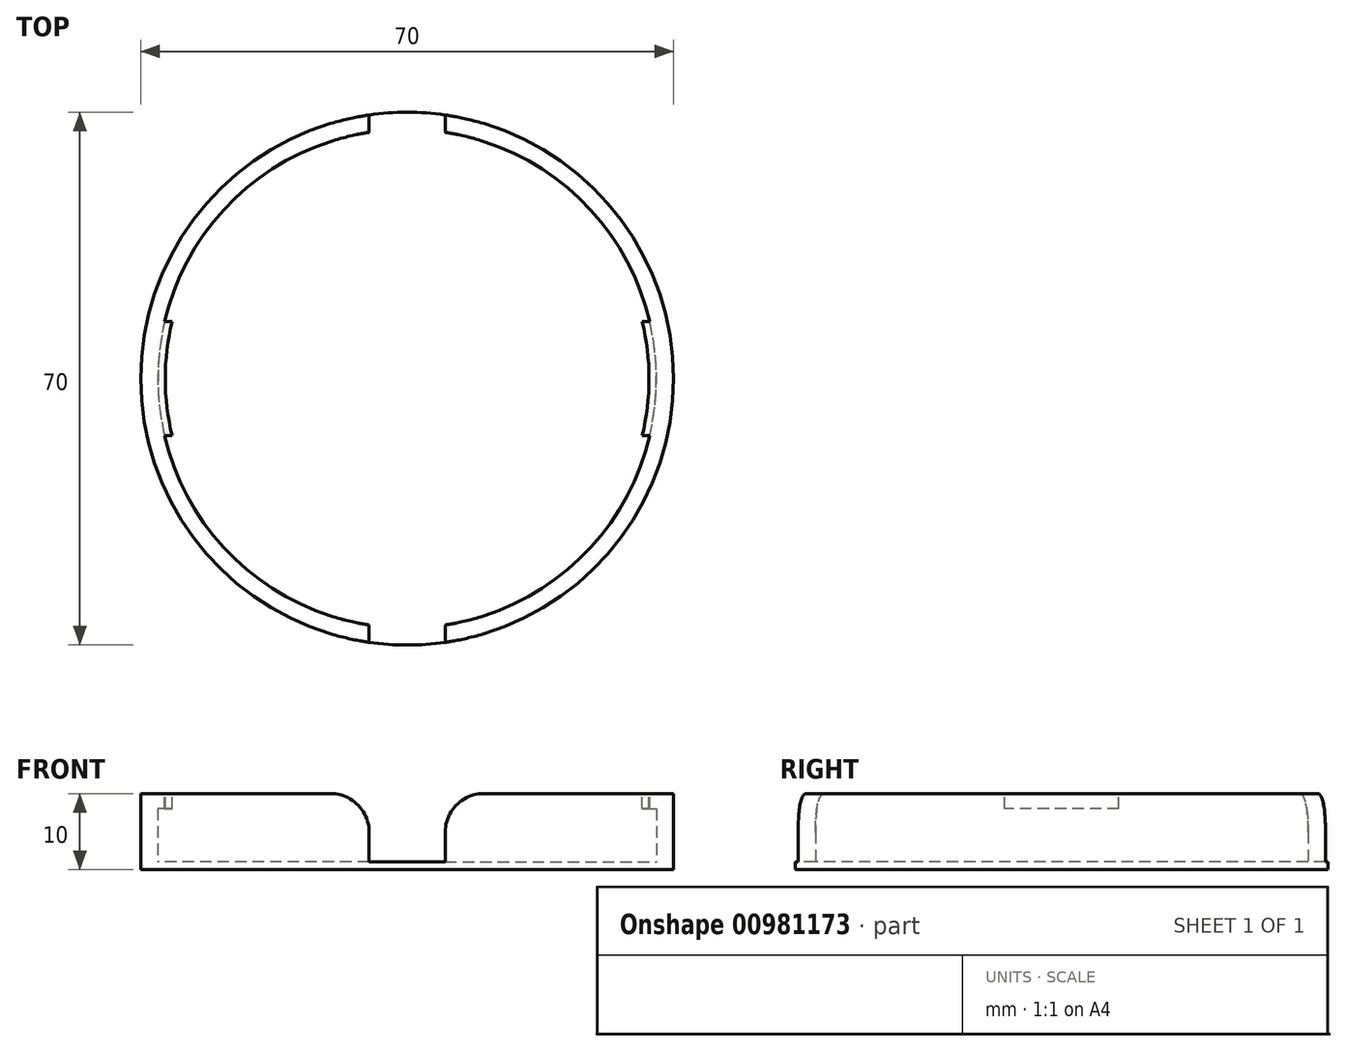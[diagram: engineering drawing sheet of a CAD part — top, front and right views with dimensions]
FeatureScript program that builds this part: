
annotation { "Feature Type Name" : "Feature", "Feature Type Description" : "" }
export const myFeature = defineFeature(function(context is Context, id is Id, definition is map)
    precondition{}
    {
        {
            var Q0;
            Q0=qCreatedBy(makeId("Top.planeOp"),FACE);
            var sketch = newSketch(context, id + "F0", { "sketchPlane" : qUnion([Q0])});
            skCircle(sketch, "E0", {"center": v(0, 0) * mm, "radius": 35 * mm});
            skSolve(sketch);
        }
        {
            var Q0;
            Q0 = qSketchRegion(id + "F0", true);
            extrude(context, id + "F1", {"entities" : qUnion([Q0]), "oppositeDirection" : true, "depth" : 1 * mm, "offsetDistance" : 25.4 * mm});
        }
        {
            var Q0;
            Q0=qCreatedBy(makeId("Top.planeOp"),FACE);
            var sketch = newSketch(context, id + "F2", { "sketchPlane" : qUnion([Q0])});
            skCircle(sketch, "E1", {"center": v(0, 0) * mm, "radius": 32.75 * mm});
            skCircle(sketch, "E2", {"center": v(0, 0) * mm, "radius": 35 * mm});
            skSolve(sketch);
        }
        {
            var Q0;
            Q0 = qSketchRegion(id + "F2", true);
            extrude(context, id + "F3", {"entities" : qUnion([Q0]), "operationType" : NewBodyOperationType.ADD, "depth" : 9 * mm, "offsetDistance" : 25.4 * mm});
        }
        {
            var Q0;
            Q0=makeQuery(id+"F3.opExtrude","CAP_FACE",FACE,{"disambiguationData":[OSD([sQuery(id+"F2.wireOp",EDGE,"E1"),sQuery(id+"F2.wireOp",EDGE,"E2")])],"isStart":false});
            var sketch = newSketch(context, id + "F4", { "sketchPlane" : qUnion([Q0])});
            skArc(sketch, "E3", {"start": v(-32.75, 0) * mm, "mid": v(-32.53, -3.78) * mm, "end": v(-31.88, -7.5) * mm});
            skLineSegment(sketch, "E4", {"start": v(-32.75, 0) * mm, "end": v(0, 0) * mm, "construction": true});
            skArc(sketch, "E5.MirrorCS", {"start": v(-32.75, 0) * mm, "mid": v(-32.53, 3.78) * mm, "end": v(-31.88, 7.5) * mm});
            skArc(sketch, "E6", {"start": v(-30.88, 7.5) * mm, "mid": v(-31.78, 0) * mm, "end": v(-30.88, -7.5) * mm});
            skLineSegment(sketch, "E7", {"start": v(-31.88, 7.5) * mm, "end": v(-30.88, 7.5) * mm});
            skLineSegment(sketch, "E8", {"start": v(-31.88, -7.5) * mm, "end": v(-30.88, -7.5) * mm});
            skLineSegment(sketch, "E9", {"start": v(0, 0) * mm, "end": v(0, 32.75) * mm, "construction": true});
            skLineSegment(sketch, "E10.MirrorCS", {"start": v(31.88, -7.5) * mm, "end": v(30.88, -7.5) * mm});
            skArc(sketch, "E11.MirrorCS", {"start": v(32.75, 0) * mm, "mid": v(32.53, -3.78) * mm, "end": v(31.88, -7.5) * mm});
            skArc(sketch, "E12.MirrorCS", {"start": v(32.75, 0) * mm, "mid": v(32.53, 3.78) * mm, "end": v(31.88, 7.5) * mm});
            skArc(sketch, "E13.MirrorCS", {"start": v(30.88, 7.5) * mm, "mid": v(31.78, 0) * mm, "end": v(30.88, -7.5) * mm});
            skLineSegment(sketch, "E14.MirrorCS", {"start": v(31.88, 7.5) * mm, "end": v(30.88, 7.5) * mm});
            skSolve(sketch);
        }
        {
            var Q0;
            Q0 = qSketchRegion(id + "F4", true);
            extrude(context, id + "F5", {"entities" : qUnion([Q0]), "operationType" : NewBodyOperationType.ADD, "oppositeDirection" : true, "depth" : 2 * mm, "offsetDistance" : 25.4 * mm});
        }
        {
            var Q0;
            Q0=qCreatedBy(makeId("Top.planeOp"),FACE);
            var sketch = newSketch(context, id + "F6", { "sketchPlane" : qUnion([Q0])});
            skLineSegment(sketch, "E15.bottom", {"start": v(5, 38.1) * mm, "end": v(-5, 38.1) * mm});
            skLineSegment(sketch, "E15.top", {"start": v(5, -38.1) * mm, "end": v(-5, -38.1) * mm});
            skLineSegment(sketch, "E15.left", {"start": v(5, 38.1) * mm, "end": v(5, -38.1) * mm});
            skLineSegment(sketch, "E15.right", {"start": v(-5, 38.1) * mm, "end": v(-5, -38.1) * mm});
            skPoint(sketch, "E15.middle", {"position": v(0, 0) * mm});
            skSolve(sketch);
        }
        {
            var Q0;
            Q0 = qSketchRegion(id + "F6", true);
            extrude(context, id + "F7", {"entities" : qUnion([Q0]), "operationType" : NewBodyOperationType.REMOVE, "depth" : 25.4 * mm, "offsetDistance" : 25.4 * mm});
        }
        {
            var Q0;
            Q0=makeQuery(id+"F7.boolean.opBoolean","INTERSECT",EDGE,{"disambiguationData":[OD(0.0)],"derivedFrom":[makeQuery(id+"F5.boolean.opBoolean","MERGE",FACE,{"derivedFrom":[makeQuery(id+"F3.opExtrude","CAP_FACE",FACE,{"disambiguationData":[OSD([sQuery(id+"F2.wireOp",EDGE,"E1"),sQuery(id+"F2.wireOp",EDGE,"E2")])],"isStart":false}),makeQuery(id+"F5.opExtrude","CAP_FACE",FACE,{"disambiguationData":[OSD([sQuery(id+"F4.wireOp",EDGE,"E3"),sQuery(id+"F4.wireOp",EDGE,"E5.MirrorCS"),sQuery(id+"F4.wireOp",EDGE,"E6"),sQuery(id+"F4.wireOp",EDGE,"E7"),sQuery(id+"F4.wireOp",EDGE,"E8")])],"isStart":true}),makeQuery(id+"F5.opExtrude","CAP_FACE",FACE,{"disambiguationData":[OSD([sQuery(id+"F4.wireOp",EDGE,"E10.MirrorCS"),sQuery(id+"F4.wireOp",EDGE,"E11.MirrorCS"),sQuery(id+"F4.wireOp",EDGE,"E12.MirrorCS"),sQuery(id+"F4.wireOp",EDGE,"E13.MirrorCS"),sQuery(id+"F4.wireOp",EDGE,"E14.MirrorCS")])],"isStart":true})]}),makeQuery(id+"F7.opExtrude","SWEPT_FACE",FACE,{"disambiguationData":[OSD([sQuery(id+"F6.wireOp",EDGE,"E15.right")])]})]});
            var Q1;
            Q1=makeQuery(id+"F7.boolean.opBoolean","INTERSECT",EDGE,{"disambiguationData":[OD(0.0)],"derivedFrom":[makeQuery(id+"F5.boolean.opBoolean","MERGE",FACE,{"derivedFrom":[makeQuery(id+"F3.opExtrude","CAP_FACE",FACE,{"disambiguationData":[OSD([sQuery(id+"F2.wireOp",EDGE,"E1"),sQuery(id+"F2.wireOp",EDGE,"E2")])],"isStart":false}),makeQuery(id+"F5.opExtrude","CAP_FACE",FACE,{"disambiguationData":[OSD([sQuery(id+"F4.wireOp",EDGE,"E3"),sQuery(id+"F4.wireOp",EDGE,"E5.MirrorCS"),sQuery(id+"F4.wireOp",EDGE,"E6"),sQuery(id+"F4.wireOp",EDGE,"E7"),sQuery(id+"F4.wireOp",EDGE,"E8")])],"isStart":true}),makeQuery(id+"F5.opExtrude","CAP_FACE",FACE,{"disambiguationData":[OSD([sQuery(id+"F4.wireOp",EDGE,"E10.MirrorCS"),sQuery(id+"F4.wireOp",EDGE,"E11.MirrorCS"),sQuery(id+"F4.wireOp",EDGE,"E12.MirrorCS"),sQuery(id+"F4.wireOp",EDGE,"E13.MirrorCS"),sQuery(id+"F4.wireOp",EDGE,"E14.MirrorCS")])],"isStart":true})]}),makeQuery(id+"F7.opExtrude","SWEPT_FACE",FACE,{"disambiguationData":[OSD([sQuery(id+"F6.wireOp",EDGE,"E15.left")])]})]});
            var Q2;
            Q2=makeQuery(id+"F7.boolean.opBoolean","INTERSECT",EDGE,{"disambiguationData":[OD(1.0)],"derivedFrom":[makeQuery(id+"F5.boolean.opBoolean","MERGE",FACE,{"derivedFrom":[makeQuery(id+"F3.opExtrude","CAP_FACE",FACE,{"disambiguationData":[OSD([sQuery(id+"F2.wireOp",EDGE,"E1"),sQuery(id+"F2.wireOp",EDGE,"E2")])],"isStart":false}),makeQuery(id+"F5.opExtrude","CAP_FACE",FACE,{"disambiguationData":[OSD([sQuery(id+"F4.wireOp",EDGE,"E3"),sQuery(id+"F4.wireOp",EDGE,"E5.MirrorCS"),sQuery(id+"F4.wireOp",EDGE,"E6"),sQuery(id+"F4.wireOp",EDGE,"E7"),sQuery(id+"F4.wireOp",EDGE,"E8")])],"isStart":true}),makeQuery(id+"F5.opExtrude","CAP_FACE",FACE,{"disambiguationData":[OSD([sQuery(id+"F4.wireOp",EDGE,"E10.MirrorCS"),sQuery(id+"F4.wireOp",EDGE,"E11.MirrorCS"),sQuery(id+"F4.wireOp",EDGE,"E12.MirrorCS"),sQuery(id+"F4.wireOp",EDGE,"E13.MirrorCS"),sQuery(id+"F4.wireOp",EDGE,"E14.MirrorCS")])],"isStart":true})]}),makeQuery(id+"F7.opExtrude","SWEPT_FACE",FACE,{"disambiguationData":[OSD([sQuery(id+"F6.wireOp",EDGE,"E15.right")])]})]});
            var Q3;
            Q3=makeQuery(id+"F7.boolean.opBoolean","INTERSECT",EDGE,{"disambiguationData":[OD(1.0)],"derivedFrom":[makeQuery(id+"F5.boolean.opBoolean","MERGE",FACE,{"derivedFrom":[makeQuery(id+"F3.opExtrude","CAP_FACE",FACE,{"disambiguationData":[OSD([sQuery(id+"F2.wireOp",EDGE,"E1"),sQuery(id+"F2.wireOp",EDGE,"E2")])],"isStart":false}),makeQuery(id+"F5.opExtrude","CAP_FACE",FACE,{"disambiguationData":[OSD([sQuery(id+"F4.wireOp",EDGE,"E3"),sQuery(id+"F4.wireOp",EDGE,"E5.MirrorCS"),sQuery(id+"F4.wireOp",EDGE,"E6"),sQuery(id+"F4.wireOp",EDGE,"E7"),sQuery(id+"F4.wireOp",EDGE,"E8")])],"isStart":true}),makeQuery(id+"F5.opExtrude","CAP_FACE",FACE,{"disambiguationData":[OSD([sQuery(id+"F4.wireOp",EDGE,"E10.MirrorCS"),sQuery(id+"F4.wireOp",EDGE,"E11.MirrorCS"),sQuery(id+"F4.wireOp",EDGE,"E12.MirrorCS"),sQuery(id+"F4.wireOp",EDGE,"E13.MirrorCS"),sQuery(id+"F4.wireOp",EDGE,"E14.MirrorCS")])],"isStart":true})]}),makeQuery(id+"F7.opExtrude","SWEPT_FACE",FACE,{"disambiguationData":[OSD([sQuery(id+"F6.wireOp",EDGE,"E15.left")])]})]});
            fillet(context, id + "F8", {"entities" : qUnion([Q0, Q1, Q2, Q3]), "radius" : 5.08 * mm, "tangentPropagation" : true, "allowEdgeOverflow" : false});
        }
    });
